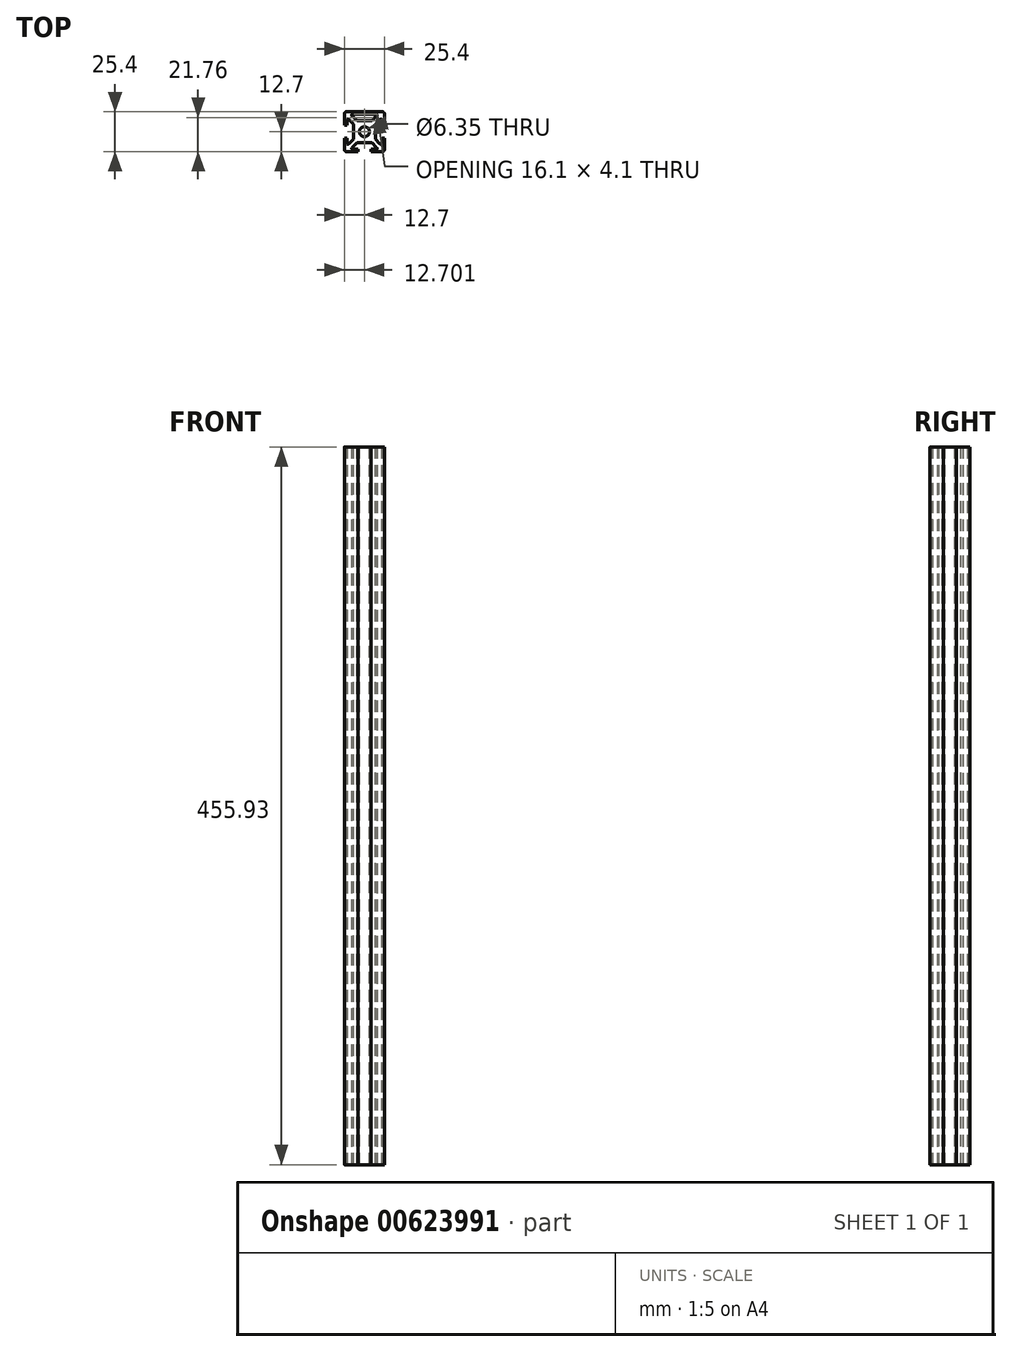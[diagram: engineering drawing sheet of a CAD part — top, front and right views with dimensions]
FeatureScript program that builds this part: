
annotation { "Feature Type Name" : "Feature", "Feature Type Description" : "" }
export const myFeature = defineFeature(function(context is Context, id is Id, definition is map)
    precondition{}
    {
        {
            var Q0;
            Q0=qCreatedBy(makeId("Top.planeOp"),FACE);
            var sketch = newSketch(context, id + "F0", { "sketchPlane" : qUnion([Q0])});
            skLineSegment(sketch, "E0.bottom", {"start": v(12.7, 12.7) * mm, "end": v(-12.7, 12.7) * mm});
            skLineSegment(sketch, "E0.top", {"start": v(12.7, -12.7) * mm, "end": v(-12.7, -12.7) * mm});
            skLineSegment(sketch, "E0.left", {"start": v(12.7, 12.7) * mm, "end": v(12.7, -12.7) * mm});
            skLineSegment(sketch, "E0.right", {"start": v(-12.7, 12.7) * mm, "end": v(-12.7, -12.7) * mm});
            skPoint(sketch, "E0.middle", {"position": v(0, 0) * mm});
            skSolve(sketch);
        }
        {
            var Q0;
            Q0=makeQuery(id+"F0.imprint","IMPRINT",FACE,{"disambiguationData":[TD([[makeQuery(id+"F0.imprint","IMPRINT",EDGE,{"derivedFrom":sQuery(id+"F0.wireOp",EDGE,"E0.bottom")}),1.0]])]});
            extrude(context, id + "F1", {"entities" : qUnion([Q0]), "depth" : 455.93 * mm, "offsetDistance" : 25.4 * mm});
        }
        {
            var Q0;
            Q0=makeQuery(id+"F1.opExtrude","CAP_FACE",FACE,{"disambiguationData":[OSD([sQuery(id+"F0.wireOp",EDGE,"E0.bottom"),sQuery(id+"F0.wireOp",EDGE,"E0.top"),sQuery(id+"F0.wireOp",EDGE,"E0.left"),sQuery(id+"F0.wireOp",EDGE,"E0.right")])],"isStart":false});
            var sketch = newSketch(context, id + "F2", { "sketchPlane" : qUnion([Q0])});
            skLineSegment(sketch, "E1", {"start": v(-7, 4.76) * mm, "end": v(-7, -4.76) * mm});
            skLineSegment(sketch, "E2", {"start": v(-7, -4.76) * mm, "end": v(-11.11, -8.87) * mm});
            skLineSegment(sketch, "E3", {"start": v(-11.11, -8.87) * mm, "end": v(-11.11, -4.1) * mm});
            skLineSegment(sketch, "E4", {"start": v(-11.11, -4.1) * mm, "end": v(-12.7, -4.1) * mm});
            skLineSegment(sketch, "E5", {"start": v(-12.7, -4.1) * mm, "end": v(-12.7, 4.1) * mm});
            skLineSegment(sketch, "E6", {"start": v(-12.7, 4.1) * mm, "end": v(-11.11, 4.1) * mm});
            skLineSegment(sketch, "E7", {"start": v(-11.11, 4.1) * mm, "end": v(-11.11, 8.87) * mm});
            skLineSegment(sketch, "E8", {"start": v(-11.11, 8.87) * mm, "end": v(-7, 4.76) * mm});
            skLineSegment(sketch, "E9", {"start": v(-4.1, -12.7) * mm, "end": v(-4.1, -11.11) * mm});
            skLineSegment(sketch, "E10", {"start": v(-4.1, -11.11) * mm, "end": v(-8.87, -11.11) * mm});
            skLineSegment(sketch, "E11", {"start": v(-8.87, -11.11) * mm, "end": v(-4.76, -7) * mm});
            skLineSegment(sketch, "E12", {"start": v(-4.76, -7) * mm, "end": v(4.76, -7) * mm});
            skLineSegment(sketch, "E13", {"start": v(4.76, -7) * mm, "end": v(8.87, -11.11) * mm});
            skLineSegment(sketch, "E14", {"start": v(8.87, -11.11) * mm, "end": v(4.1, -11.11) * mm});
            skLineSegment(sketch, "E15", {"start": v(4.1, -11.11) * mm, "end": v(4.1, -12.7) * mm});
            skLineSegment(sketch, "E16", {"start": v(4.1, -12.7) * mm, "end": v(-4.1, -12.7) * mm});
            skLineSegment(sketch, "E17", {"start": v(12.7, -4.1) * mm, "end": v(11.11, -4.1) * mm});
            skLineSegment(sketch, "E18", {"start": v(11.11, -4.1) * mm, "end": v(11.11, -8.87) * mm});
            skLineSegment(sketch, "E19", {"start": v(11.11, -8.87) * mm, "end": v(7, -4.76) * mm});
            skLineSegment(sketch, "E20", {"start": v(7, -4.76) * mm, "end": v(7, 4.76) * mm});
            skLineSegment(sketch, "E21", {"start": v(7, 4.76) * mm, "end": v(11.11, 8.87) * mm});
            skLineSegment(sketch, "E22", {"start": v(11.11, 8.87) * mm, "end": v(11.11, 4.1) * mm});
            skLineSegment(sketch, "E23", {"start": v(11.11, 4.1) * mm, "end": v(12.7, 4.1) * mm});
            skLineSegment(sketch, "E24", {"start": v(12.7, 4.1) * mm, "end": v(12.7, -4.1) * mm});
            skLineSegment(sketch, "E25", {"start": v(-4.1, 12.7) * mm, "end": v(-4.1, 11.11) * mm});
            skLineSegment(sketch, "E26", {"start": v(-4.1, 11.11) * mm, "end": v(-8.87, 11.11) * mm});
            skLineSegment(sketch, "E27", {"start": v(-8.87, 11.11) * mm, "end": v(-4.76, 7) * mm});
            skLineSegment(sketch, "E28", {"start": v(-4.76, 7) * mm, "end": v(4.76, 7) * mm});
            skLineSegment(sketch, "E29", {"start": v(4.76, 7) * mm, "end": v(8.87, 11.11) * mm});
            skLineSegment(sketch, "E30", {"start": v(8.87, 11.11) * mm, "end": v(4.1, 11.11) * mm});
            skLineSegment(sketch, "E31", {"start": v(4.1, 11.11) * mm, "end": v(4.1, 12.7) * mm});
            skLineSegment(sketch, "E32", {"start": v(4.1, 12.7) * mm, "end": v(-4.1, 12.7) * mm});
            skSolve(sketch);
        }
        {
            var Q0;
            Q0=makeQuery(id+"F2.imprint","IMPRINT",FACE,{"disambiguationData":[TD([[makeQuery(id+"F2.imprint","IMPRINT",EDGE,{"derivedFrom":sQuery(id+"F2.wireOp",EDGE,"E1")}),-1.0]])]});
            var Q1;
            Q1=makeQuery(id+"F2.imprint","IMPRINT",FACE,{"disambiguationData":[TD([[makeQuery(id+"F2.imprint","IMPRINT",EDGE,{"derivedFrom":sQuery(id+"F2.wireOp",EDGE,"E25")}),1.0]])]});
            var Q2;
            Q2=makeQuery(id+"F2.imprint","IMPRINT",FACE,{"disambiguationData":[TD([[makeQuery(id+"F2.imprint","IMPRINT",EDGE,{"derivedFrom":sQuery(id+"F2.wireOp",EDGE,"E17")}),-1.0]])]});
            var Q3;
            Q3=makeQuery(id+"F2.imprint","IMPRINT",FACE,{"disambiguationData":[TD([[makeQuery(id+"F2.imprint","IMPRINT",EDGE,{"derivedFrom":sQuery(id+"F2.wireOp",EDGE,"E9")}),-1.0]])]});
            extrude(context, id + "F3", {"entities" : qUnion([Q0, Q1, Q2, Q3]), "operationType" : NewBodyOperationType.REMOVE, "oppositeDirection" : true, "depth" : 455.93 * mm, "offsetDistance" : 25.4 * mm});
        }
        {
            var Q0;
            Q0=makeQuery(id+"F1.opExtrude","CAP_FACE",FACE,{"disambiguationData":[OSD([sQuery(id+"F0.wireOp",EDGE,"E0.bottom"),sQuery(id+"F0.wireOp",EDGE,"E0.top"),sQuery(id+"F0.wireOp",EDGE,"E0.left"),sQuery(id+"F0.wireOp",EDGE,"E0.right")])],"isStart":false});
            var sketch = newSketch(context, id + "F4", { "sketchPlane" : qUnion([Q0])});
            skCircle(sketch, "E33", {"center": v(0, 0) * mm, "radius": 3.18 * mm});
            skSolve(sketch);
        }
        {
            var Q0;
            Q0=makeQuery(id+"F4.imprint","IMPRINT",FACE,{"disambiguationData":[TD([[makeQuery(id+"F4.imprint","IMPRINT",EDGE,{"derivedFrom":sQuery(id+"F4.wireOp",EDGE,"E33")}),1.0]])]});
            extrude(context, id + "F5", {"entities" : qUnion([Q0]), "operationType" : NewBodyOperationType.REMOVE, "oppositeDirection" : true, "depth" : 455.93 * mm, "offsetDistance" : 25.4 * mm});
        }
        {
            var Q0;
            Q0=makeQuery(id+"F1.opExtrude","SWEPT_EDGE",EDGE,{"disambiguationData":[OSD([sQuery(id+"F0.wireOp",EDGE,"E0.bottom"),sQuery(id+"F0.wireOp",EDGE,"E0.right")])]});
            var Q1;
            Q1=makeQuery(id+"F1.opExtrude","SWEPT_EDGE",EDGE,{"disambiguationData":[OSD([sQuery(id+"F0.wireOp",EDGE,"E0.bottom"),sQuery(id+"F0.wireOp",EDGE,"E0.left")])]});
            var Q2;
            Q2=makeQuery(id+"F1.opExtrude","SWEPT_EDGE",EDGE,{"disambiguationData":[OSD([sQuery(id+"F0.wireOp",EDGE,"E0.top"),sQuery(id+"F0.wireOp",EDGE,"E0.left")])]});
            var Q3;
            Q3=makeQuery(id+"F1.opExtrude","SWEPT_EDGE",EDGE,{"disambiguationData":[OSD([sQuery(id+"F0.wireOp",EDGE,"E0.top"),sQuery(id+"F0.wireOp",EDGE,"E0.right")])]});
            fillet(context, id + "F6", {"entities" : qUnion([Q0, Q1, Q2, Q3]), "radius" : 1.59 * mm, "tangentPropagation" : true, "rho" : 0.5, "crossSection" : FilletCrossSection.CONIC, "allowEdgeOverflow" : false});
        }
        {
            var Q0;
            Q0=makeQuery(id+"F3.boolean.opBoolean","COPY",EDGE,{"derivedFrom":makeQuery(id+"F3.opExtrude","SWEPT_EDGE",EDGE,{"disambiguationData":[OSD([sQuery(id+"F2.wireOp",EDGE,"E7"),sQuery(id+"F2.wireOp",EDGE,"E8")])]})});
            var Q1;
            Q1=makeQuery(id+"F3.boolean.opBoolean","COPY",EDGE,{"derivedFrom":makeQuery(id+"F3.opExtrude","SWEPT_EDGE",EDGE,{"disambiguationData":[OSD([sQuery(id+"F2.wireOp",EDGE,"E21"),sQuery(id+"F2.wireOp",EDGE,"E22")])]})});
            var Q2;
            Q2=makeQuery(id+"F3.boolean.opBoolean","COPY",EDGE,{"derivedFrom":makeQuery(id+"F3.opExtrude","SWEPT_EDGE",EDGE,{"disambiguationData":[OSD([sQuery(id+"F2.wireOp",EDGE,"E18"),sQuery(id+"F2.wireOp",EDGE,"E19")])]})});
            var Q3;
            Q3=makeQuery(id+"F3.boolean.opBoolean","COPY",EDGE,{"derivedFrom":makeQuery(id+"F3.opExtrude","SWEPT_EDGE",EDGE,{"disambiguationData":[OSD([sQuery(id+"F2.wireOp",EDGE,"E2"),sQuery(id+"F2.wireOp",EDGE,"E3")])]})});
            var Q4;
            Q4=makeQuery(id+"F3.boolean.opBoolean","COPY",EDGE,{"derivedFrom":makeQuery(id+"F3.opExtrude","SWEPT_EDGE",EDGE,{"disambiguationData":[OSD([sQuery(id+"F2.wireOp",EDGE,"E10"),sQuery(id+"F2.wireOp",EDGE,"E11")])]})});
            var Q5;
            Q5=makeQuery(id+"F3.boolean.opBoolean","COPY",EDGE,{"derivedFrom":makeQuery(id+"F3.opExtrude","SWEPT_EDGE",EDGE,{"disambiguationData":[OSD([sQuery(id+"F2.wireOp",EDGE,"E13"),sQuery(id+"F2.wireOp",EDGE,"E14")])]})});
            var Q6;
            Q6=makeQuery(id+"F3.boolean.opBoolean","COPY",EDGE,{"derivedFrom":makeQuery(id+"F3.opExtrude","SWEPT_EDGE",EDGE,{"disambiguationData":[OSD([sQuery(id+"F2.wireOp",EDGE,"E29"),sQuery(id+"F2.wireOp",EDGE,"E30")])]})});
            var Q7;
            Q7=makeQuery(id+"F3.boolean.opBoolean","COPY",EDGE,{"derivedFrom":makeQuery(id+"F3.opExtrude","SWEPT_EDGE",EDGE,{"disambiguationData":[OSD([sQuery(id+"F2.wireOp",EDGE,"E26"),sQuery(id+"F2.wireOp",EDGE,"E27")])]})});
            fillet(context, id + "F7", {"entities" : qUnion([Q0, Q1, Q2, Q3, Q4, Q5, Q6, Q7]), "radius" : 0.8 * mm, "tangentPropagation" : true, "rho" : 0.5, "crossSection" : FilletCrossSection.CONIC, "allowEdgeOverflow" : false});
        }
        {
            var Q0;
            Q0=makeQuery(id+"F1.opExtrude","CAP_FACE",FACE,{"disambiguationData":[OSD([sQuery(id+"F0.wireOp",EDGE,"E0.bottom"),sQuery(id+"F0.wireOp",EDGE,"E0.top"),sQuery(id+"F0.wireOp",EDGE,"E0.left"),sQuery(id+"F0.wireOp",EDGE,"E0.right")])],"isStart":false});
            var sketch = newSketch(context, id + "F8", { "sketchPlane" : qUnion([Q0])});
            skLineSegment(sketch, "E34.bottom", {"start": v(-4.1, 12.7) * mm, "end": v(4.1, 12.7) * mm});
            skLineSegment(sketch, "E34.top", {"start": v(-4.1, 11.11) * mm, "end": v(4.1, 11.11) * mm});
            skLineSegment(sketch, "E34.left", {"start": v(-4.1, 12.7) * mm, "end": v(-4.1, 11.11) * mm});
            skLineSegment(sketch, "E34.right", {"start": v(4.1, 12.7) * mm, "end": v(4.1, 11.11) * mm});
            skSolve(sketch);
        }
        {
            var Q0;
            Q0=makeQuery(id+"F8.imprint","IMPRINT",FACE,{"disambiguationData":[TD([[makeQuery(id+"F8.imprint","IMPRINT",EDGE,{"derivedFrom":sQuery(id+"F8.wireOp",EDGE,"E34.bottom")}),-1.0]])]});
            extrude(context, id + "F9", {"entities" : qUnion([Q0]), "operationType" : NewBodyOperationType.ADD, "oppositeDirection" : true, "depth" : 455.93 * mm, "offsetDistance" : 25.4 * mm});
        }
    });
